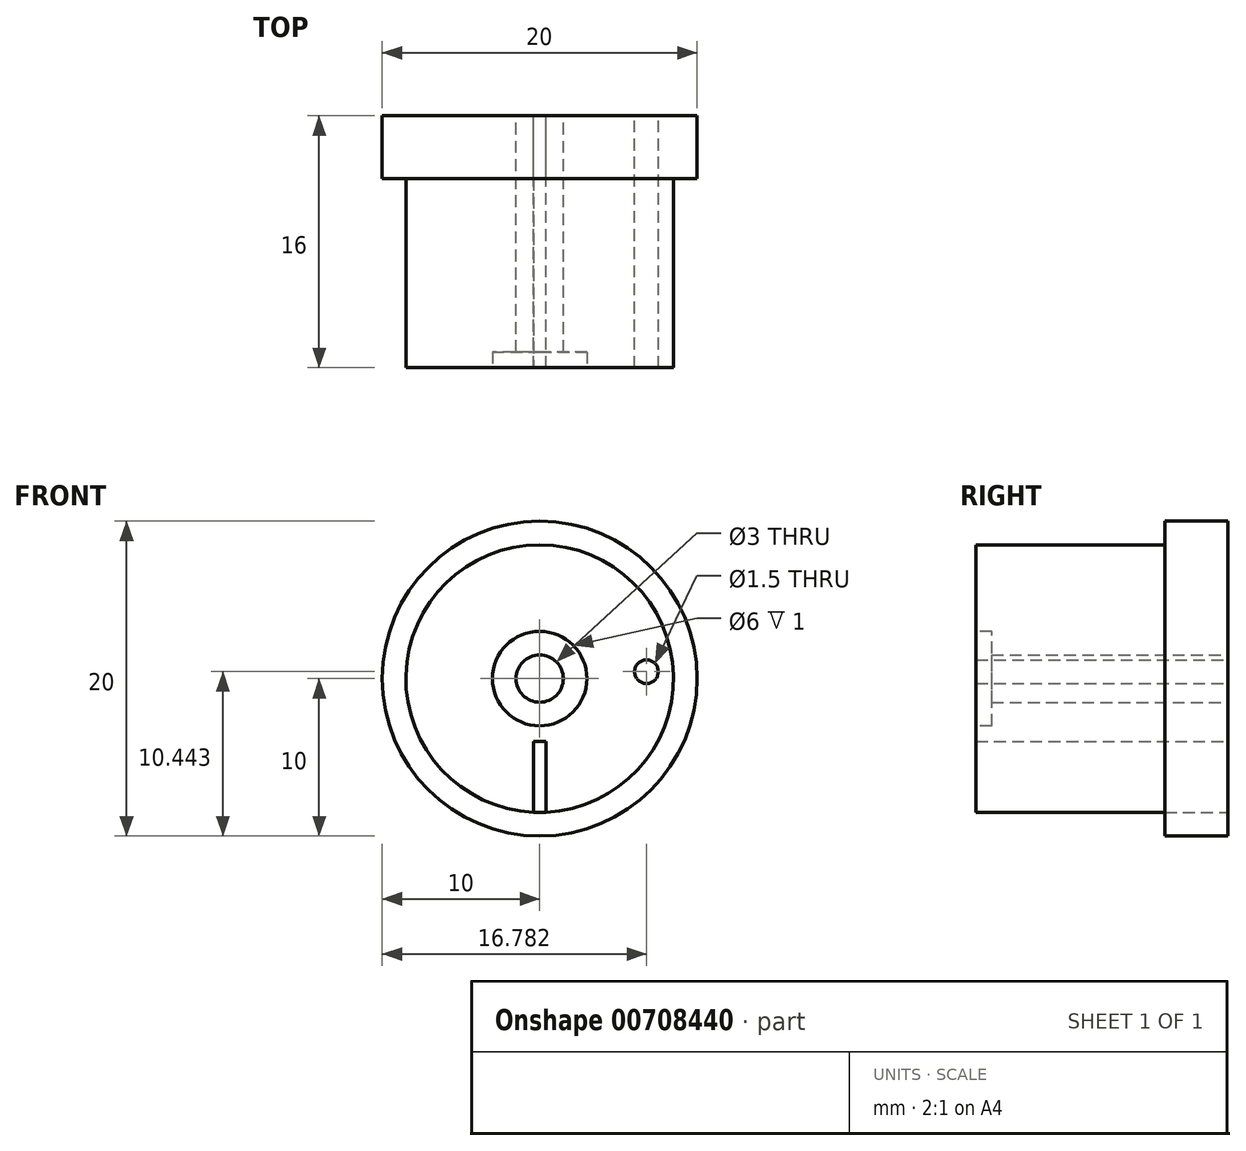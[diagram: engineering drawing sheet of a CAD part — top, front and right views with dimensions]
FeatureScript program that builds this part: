
annotation { "Feature Type Name" : "Feature", "Feature Type Description" : "" }
export const myFeature = defineFeature(function(context is Context, id is Id, definition is map)
    precondition{}
    {
        {
            var Q0;
            Q0=qCreatedBy(makeId("Front.planeOp"),FACE);
            var sketch = newSketch(context, id + "F0", { "sketchPlane" : qUnion([Q0])});
            skCircle(sketch, "E0", {"center": v(0, 0) * mm, "radius": 10 * mm});
            skSolve(sketch);
        }
        {
            var Q0;
            Q0=qSketchRegion(id+"F0",true);
            extrude(context, id + "F1", {"entities" : qUnion([Q0]), "depth" : 4 * mm, "offsetDistance" : 25 * mm});
        }
        {
            var Q0;
            Q0=makeQuery(id+"F1.opExtrude","CAP_FACE",FACE,{"disambiguationData":[OSD([sQuery(id+"F0.wireOp",EDGE,"E0")])],"isStart":false});
            var sketch = newSketch(context, id + "F2", { "sketchPlane" : qUnion([Q0])});
            skCircle(sketch, "E1", {"center": v(0, 0) * mm, "radius": 8.5 * mm});
            skSolve(sketch);
        }
        {
            var Q0;
            Q0=qSketchRegion(id+"F2",true);
            extrude(context, id + "F3", {"entities" : qUnion([Q0]), "operationType" : NewBodyOperationType.ADD, "depth" : 12 * mm, "offsetDistance" : 25 * mm});
        }
        {
            var Q0;
            Q0=makeQuery(id+"F1.opExtrude","CAP_FACE",FACE,{"disambiguationData":[OSD([sQuery(id+"F0.wireOp",EDGE,"E0")])],"isStart":true});
            var sketch = newSketch(context, id + "F4", { "sketchPlane" : qUnion([Q0])});
            skLineSegment(sketch, "E2.bottom", {"start": v(-0.4, -4) * mm, "end": v(0.4, -4) * mm});
            skLineSegment(sketch, "E2.top", {"start": v(-0.4, -8.5) * mm, "end": v(0.4, -8.5) * mm});
            skLineSegment(sketch, "E2.left", {"start": v(-0.4, -4) * mm, "end": v(-0.4, -8.5) * mm});
            skLineSegment(sketch, "E2.right", {"start": v(0.4, -4) * mm, "end": v(0.4, -8.5) * mm});
            skSolve(sketch);
        }
        {
            var Q0;
            Q0=qSketchRegion(id+"F4",true);
            extrude(context, id + "F5", {"entities" : qUnion([Q0]), "operationType" : NewBodyOperationType.REMOVE, "endBound" : BoundingType.THROUGH_ALL, "oppositeDirection" : true, "depth" : 25 * mm, "offsetDistance" : 25 * mm});
        }
        {
            var Q0;
            Q0=makeQuery(id+"F1.opExtrude","CAP_FACE",FACE,{"disambiguationData":[OSD([sQuery(id+"F0.wireOp",EDGE,"E0")])],"isStart":true});
            var sketch = newSketch(context, id + "F6", { "sketchPlane" : qUnion([Q0])});
            skCircle(sketch, "E3", {"center": v(0, 0) * mm, "radius": 1.5 * mm});
            skSolve(sketch);
        }
        {
            var Q0;
            Q0=qSketchRegion(id+"F6",true);
            extrude(context, id + "F7", {"entities" : qUnion([Q0]), "operationType" : NewBodyOperationType.REMOVE, "endBound" : BoundingType.THROUGH_ALL, "oppositeDirection" : true, "depth" : 25 * mm, "offsetDistance" : 25 * mm});
        }
        {
            var Q0;
            Q0=makeQuery(id+"F1.opExtrude","CAP_FACE",FACE,{"disambiguationData":[OSD([sQuery(id+"F0.wireOp",EDGE,"E0")])],"isStart":true});
            var sketch = newSketch(context, id + "F8", { "sketchPlane" : qUnion([Q0])});
            skCircle(sketch, "E4", {"center": v(-6.78, 0.44) * mm, "radius": 0.75 * mm});
            skSolve(sketch);
        }
        {
            var Q0;
            Q0=qSketchRegion(id+"F8",true);
            extrude(context, id + "F9", {"entities" : qUnion([Q0]), "operationType" : NewBodyOperationType.REMOVE, "oppositeDirection" : true, "depth" : 25 * mm, "offsetDistance" : 25 * mm});
        }
        {
            var Q0;
            Q0=makeQuery(id+"F3.opExtrude","CAP_FACE",FACE,{"disambiguationData":[OSD([sQuery(id+"F2.wireOp",EDGE,"E1")])],"isStart":false});
            var sketch = newSketch(context, id + "F10", { "sketchPlane" : qUnion([Q0])});
            skCircle(sketch, "E5", {"center": v(0, 0) * mm, "radius": 3 * mm});
            skSolve(sketch);
        }
        {
            var Q0;
            Q0=makeQuery(id+"F10.imprint","IMPRINT",FACE,{"disambiguationData":[TD([[makeQuery(id+"F10.imprint","IMPRINT",EDGE,{"derivedFrom":sQuery(id+"F10.wireOp",EDGE,"E5")}),1.0]])]});
            extrude(context, id + "F11", {"entities" : qUnion([Q0]), "operationType" : NewBodyOperationType.REMOVE, "oppositeDirection" : true, "depth" : 1 * mm, "offsetDistance" : 25 * mm});
        }
    });
